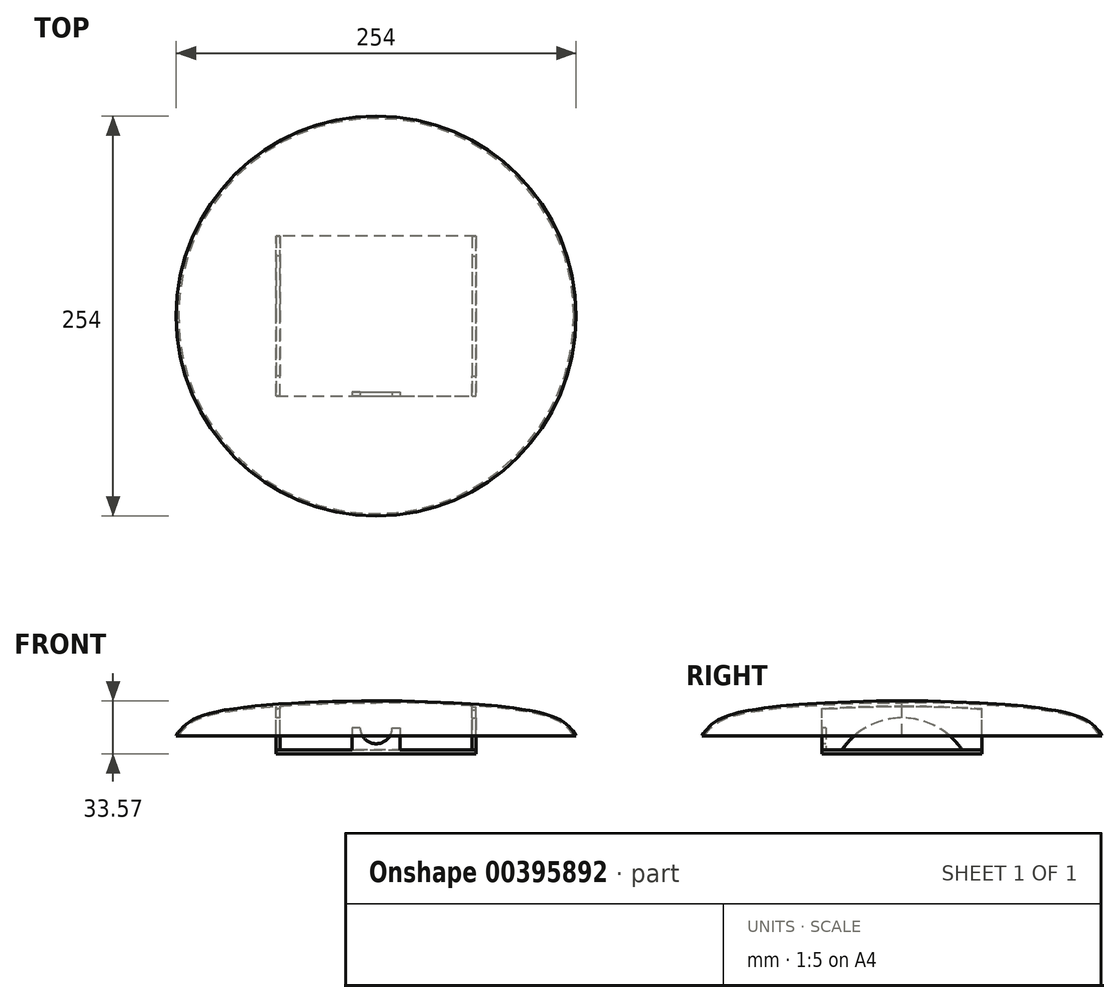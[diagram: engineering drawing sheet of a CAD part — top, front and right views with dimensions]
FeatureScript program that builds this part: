
annotation { "Feature Type Name" : "Feature", "Feature Type Description" : "" }
export const myFeature = defineFeature(function(context is Context, id is Id, definition is map)
    precondition{}
    {
        {
            var Q0;
            Q0=qCreatedBy(makeId("Front.planeOp"),FACE);
            var sketch = newSketch(context, id + "F0", { "sketchPlane" : qUnion([Q0])});
            skPoint(sketch, "E0.orphan", {"position": v(0, 0) * mm});
            skPoint(sketch, "E1.orphan", {"position": v(101.6, 0) * mm});
            skFitSpline(sketch, "E2", {"points": [v(-127, 0) * mm, v(-101.6, 15.24) * mm, v(101.6, 15.24) * mm, v(127, 0) * mm], "startDerivative": vector(60.14, 95.3) * mm, "endDerivative": vector(60.14, -95.3) * mm});
            skLineSegment(sketch, "E3", {"start": v(-127, 0) * mm, "end": v(-125.5, 0) * mm});
            skFitSpline(sketch, "E4.0", {"points": [v(-125.93, -0.68) * mm, v(-125.31, 0.3) * mm, v(-124.07, 2.14) * mm, v(-122, 4.62) * mm, v(-119.5, 6.87) * mm, v(-116.37, 8.94) * mm, v(-112.39, 10.83) * mm, v(-107.35, 12.56) * mm, v(-101.06, 14.13) * mm, v(-93.35, 15.55) * mm, v(-84.4, 16.8) * mm, v(-74.35, 17.88) * mm, v(-63.38, 18.8) * mm, v(-47.71, 19.8) * mm, v(-26.59, 20.64) * mm, v(0, 20.98) * mm, v(26.59, 20.64) * mm, v(47.71, 19.8) * mm, v(63.38, 18.8) * mm, v(74.35, 17.88) * mm, v(84.4, 16.8) * mm, v(93.35, 15.55) * mm, v(101.06, 14.13) * mm, v(107.35, 12.56) * mm, v(112.39, 10.83) * mm, v(116.37, 8.94) * mm, v(119.5, 6.87) * mm, v(122, 4.62) * mm, v(124.07, 2.14) * mm, v(125.31, 0.3) * mm, v(125.93, -0.68) * mm]});
            skLineSegment(sketch, "E5", {"start": v(0, 20.87) * mm, "end": v(0, 22.14) * mm});
            skPoint(sketch, "E6.orphan", {"position": v(-101.6, 0) * mm});
            skSolve(sketch);
        }
        {
            var Q0;
            Q0=makeQuery(id+"F0.imprint","IMPRINT",FACE,{"disambiguationData":[TD([[makeQuery(id+"F0.imprint","IMPRINT",EDGE,{"derivedFrom":sQuery(id+"F0.wireOp",EDGE,"E2")}),-1.0]])]});
            var Q1;
            Q1=sQuery(id+"F0.wireOp",EDGE,"E5");
            revolve(context, id + "F1", {"entities" : qUnion([Q0]), "axis" : qUnion([Q1]), "revolveType" : RevolveType.FULL});
        }
        {
            var Q0;
            Q0=qCreatedBy(makeId("Right.planeOp"),FACE);
            cPlane(context, id + "F2", {"entities" : qUnion([Q0]), "cplaneType" : CPlaneType.OFFSET, "offset" : 63.5 * mm, "width" : 152.4 * mm, "height" : 152.4 * mm});
        }
        {
            var Q0;
            Q0=qCreatedBy(id+"F2.planeOp",FACE);
            var sketch = newSketch(context, id + "F3", { "sketchPlane" : qUnion([Q0])});
            skLineSegment(sketch, "E7.right", {"start": v(-50.8, 0) * mm, "end": v(-50.8, -8.9) * mm});
            skLineSegment(sketch, "E8.left", {"start": v(0, -8.89) * mm, "end": v(0, -8.9) * mm});
            skLineSegment(sketch, "E8.right", {"start": v(50.8, -8.89) * mm, "end": v(50.8, -8.89) * mm});
            skLineSegment(sketch, "E9.right", {"start": v(50.8, 0) * mm, "end": v(50.8, -8.89) * mm});
            skLineSegment(sketch, "E10", {"start": v(-50.8, 0) * mm, "end": v(-50.8, 16.53) * mm});
            skLineSegment(sketch, "E11", {"start": v(50.8, 0) * mm, "end": v(50.8, 16.53) * mm});
            skArc(sketch, "E12", {"start": v(50.8, 16.53) * mm, "mid": v(0, 18.35) * mm, "end": v(-50.8, 16.53) * mm});
            skLineSegment(sketch, "E13", {"start": v(-50.8, -8.9) * mm, "end": v(-38.1, -8.9) * mm});
            skLineSegment(sketch, "E14", {"start": v(50.8, -8.89) * mm, "end": v(38.1, -8.89) * mm});
            skArc(sketch, "E15", {"start": v(38.1, -8.89) * mm, "mid": v(0, 11.36) * mm, "end": v(-38.1, -8.9) * mm});
            skLineSegment(sketch, "E16.trimOffspring", {"start": v(38.1, -8.89) * mm, "end": v(50.8, -8.89) * mm});
            skSolve(sketch);
        }
        {
            var Q0;
            Q0=qSketchRegion(id+"F3",true);
            extrude(context, id + "F4", {"entities" : qUnion([Q0]), "oppositeDirection" : true, "depth" : 2.54 * mm});
        }
        {
            var Q0;
            Q0=qCreatedBy(id+"F2.planeOp",FACE);
            cPlane(context, id + "F5", {"entities" : qUnion([Q0]), "cplaneType" : CPlaneType.OFFSET, "offset" : 127 * mm, "oppositeDirection" : true, "width" : 152.4 * mm, "height" : 152.4 * mm});
        }
        {
            var Q0;
            Q0=qCreatedBy(id+"F5.planeOp",FACE);
            var sketch = newSketch(context, id + "F6", { "sketchPlane" : qUnion([Q0])});
            skLineSegment(sketch, "E17", {"start": v(50.8, -8.9) * mm, "end": v(38.1, -8.9) * mm});
            skLineSegment(sketch, "E18", {"start": v(50.8, -8.9) * mm, "end": v(50.8, 18) * mm});
            skLineSegment(sketch, "E19", {"start": v(-50.8, -8.9) * mm, "end": v(-50.8, 18) * mm});
            skLineSegment(sketch, "E20", {"start": v(-50.8, -8.9) * mm, "end": v(-38.1, -8.9) * mm});
            skArc(sketch, "E21", {"start": v(38.1, -8.9) * mm, "mid": v(0, 11.34) * mm, "end": v(-38.1, -8.9) * mm});
            skArc(sketch, "E22", {"start": v(50.8, 18) * mm, "mid": v(0, 19.92) * mm, "end": v(-50.8, 18) * mm});
            skSolve(sketch);
        }
        {
            var Q0;
            Q0=qSketchRegion(id+"F6",true);
            extrude(context, id + "F7", {"entities" : qUnion([Q0]), "operationType" : NewBodyOperationType.ADD, "depth" : 2.54 * mm});
        }
        {
            var Q0;
            Q0=makeQuery(id+"F4.opExtrude","SWEPT_FACE",FACE,{"disambiguationData":[OSD([sQuery(id+"F3.wireOp",EDGE,"E13")])]});
            var sketch = newSketch(context, id + "F8", { "sketchPlane" : qUnion([Q0])});
            skLineSegment(sketch, "E23.left", {"start": v(63.5, 50.8) * mm, "end": v(63.5, 50.8) * mm});
            skLineSegment(sketch, "E23.right", {"start": v(-63.5, 50.8) * mm, "end": v(-63.5, 50.8) * mm});
            skLineSegment(sketch, "E24", {"start": v(63.5, 50.8) * mm, "end": v(63.5, -50.75) * mm});
            skPoint(sketch, "E24.endSnap0", {"position": v(63.5, 44.45) * mm});
            skLineSegment(sketch, "E25", {"start": v(63.5, -50.75) * mm, "end": v(-63.5, -50.82) * mm});
            skLineSegment(sketch, "E26", {"start": v(-63.5, -50.82) * mm, "end": v(-63.5, 50.8) * mm});
            skLineSegment(sketch, "E27", {"start": v(-63.5, 50.8) * mm, "end": v(63.5, 50.8) * mm});
            skSolve(sketch);
        }
        {
            var Q0;
            Q0=qSketchRegion(id+"F8",true);
            extrude(context, id + "F9", {"entities" : qUnion([Q0]), "depth" : 2.54 * mm});
        }
        {
            var Q0;
            Q0=qCreatedBy(makeId("Front.planeOp"),FACE);
            cPlane(context, id + "F10", {"entities" : qUnion([Q0]), "cplaneType" : CPlaneType.OFFSET, "offset" : 50.8 * mm, "width" : 152.4 * mm, "height" : 152.4 * mm});
        }
        {
            var Q0;
            Q0=qCreatedBy(id+"F10.planeOp",FACE);
            var sketch = newSketch(context, id + "F11", { "sketchPlane" : qUnion([Q0])});
            skArc(sketch, "E28", {"start": v(-10.16, 5.08) * mm, "mid": v(0, -5.08) * mm, "end": v(10.16, 5.08) * mm});
            skLineSegment(sketch, "E29", {"start": v(-10.16, 5.08) * mm, "end": v(-15.24, 5.08) * mm});
            skLineSegment(sketch, "E30", {"start": v(-15.24, 5.08) * mm, "end": v(-15.24, -8.9) * mm});
            skLineSegment(sketch, "E31", {"start": v(10.16, 5.08) * mm, "end": v(15.24, 5.08) * mm});
            skLineSegment(sketch, "E32", {"start": v(15.24, 5.08) * mm, "end": v(15.24, -8.9) * mm});
            skPoint(sketch, "E33.orphan", {"position": v(0, 0) * mm});
            skLineSegment(sketch, "E34", {"start": v(-15.24, -8.9) * mm, "end": v(15.24, -8.9) * mm});
            skSolve(sketch);
        }
        {
            var Q0;
            Q0=qSketchRegion(id+"F11",true);
            extrude(context, id + "F12", {"entities" : qUnion([Q0]), "operationType" : NewBodyOperationType.ADD, "oppositeDirection" : true, "depth" : 2.54 * mm});
        }
    });
